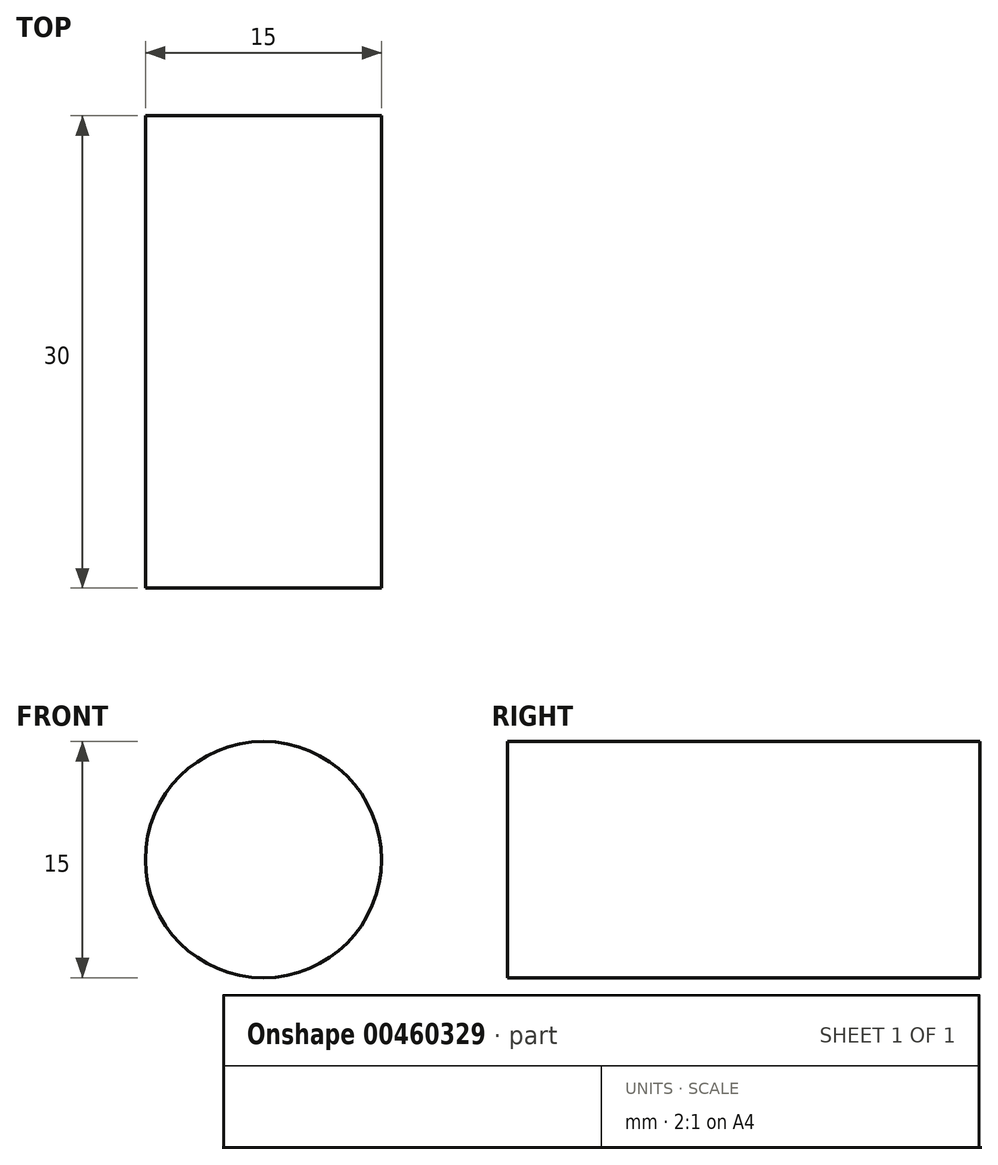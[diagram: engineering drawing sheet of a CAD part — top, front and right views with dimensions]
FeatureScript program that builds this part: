
annotation { "Feature Type Name" : "Feature", "Feature Type Description" : "" }
export const myFeature = defineFeature(function(context is Context, id is Id, definition is map)
    precondition{}
    {
        {
            var Q0;
            Q0=qCreatedBy(makeId("Front.planeOp"),FACE);
            var sketch = newSketch(context, id + "F0", { "sketchPlane" : qUnion([Q0])});
            skCircle(sketch, "E0", {"center": v(0, 0) * mm, "radius": 7.5 * mm});
            skSolve(sketch);
        }
        {
            var Q0;
            Q0 = qSketchRegion(id + "F0", true);
            extrude(context, id + "F1", {"entities" : qUnion([Q0]), "depth" : 30 * mm});
        }
    });
